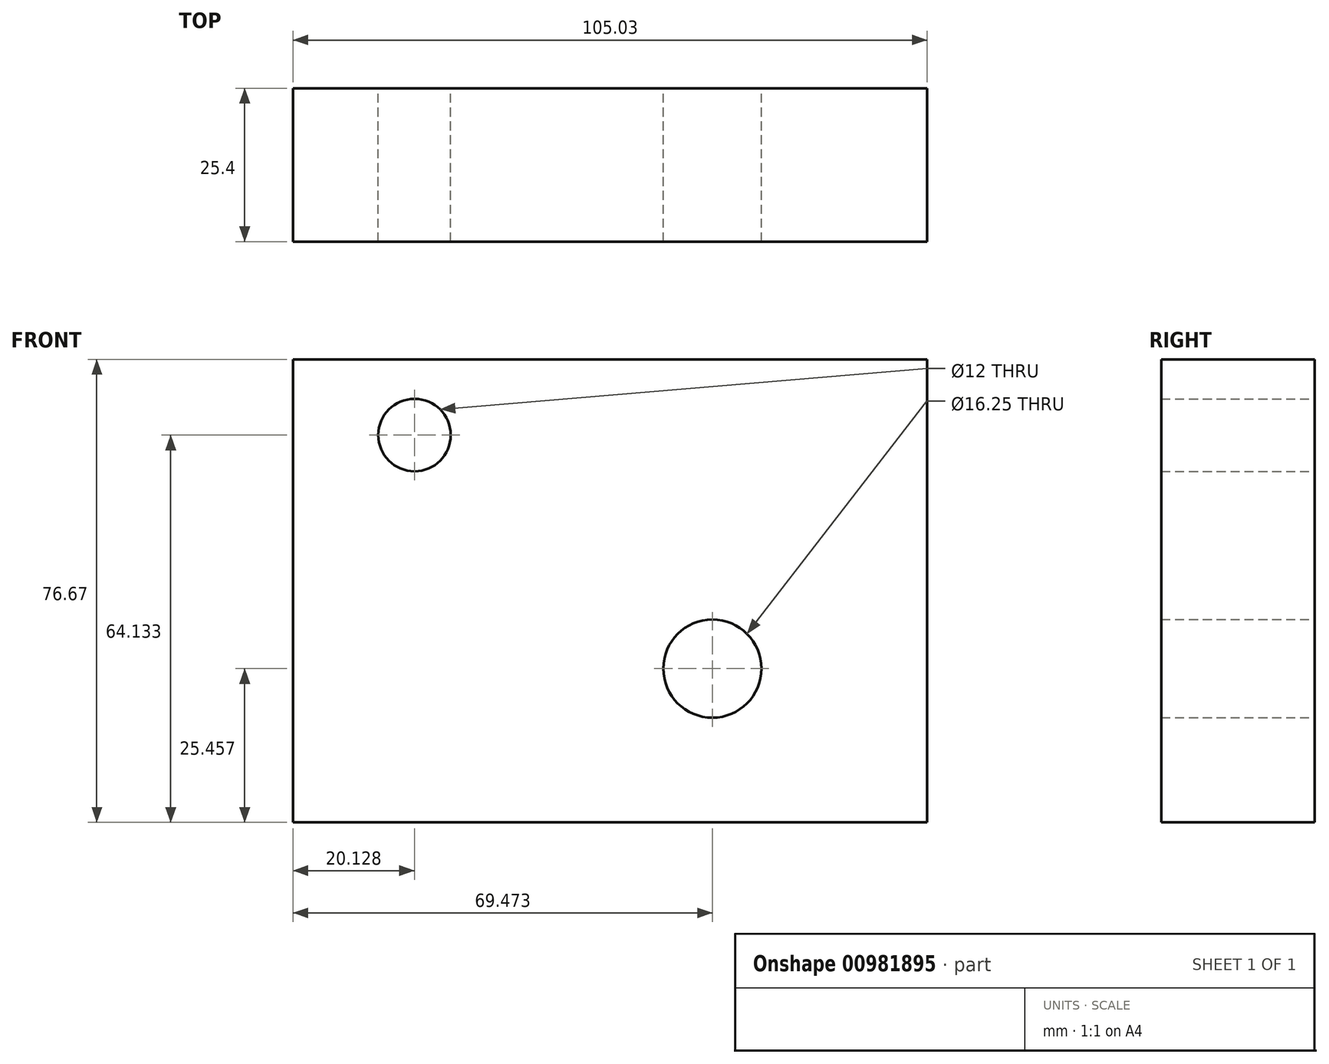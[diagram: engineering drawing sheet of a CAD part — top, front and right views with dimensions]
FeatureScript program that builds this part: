
annotation { "Feature Type Name" : "Feature", "Feature Type Description" : "" }
export const myFeature = defineFeature(function(context is Context, id is Id, definition is map)
    precondition{}
    {
        {
            var Q0;
            Q0=qCreatedBy(makeId("Front.planeOp"),FACE);
            var sketch = newSketch(context, id + "F0", { "sketchPlane" : qUnion([Q0])});
            skLineSegment(sketch, "E0.bottom", {"start": v(-51.98, 36.51) * mm, "end": v(53.05, 36.51) * mm});
            skLineSegment(sketch, "E0.top", {"start": v(-51.98, -40.16) * mm, "end": v(53.05, -40.16) * mm});
            skLineSegment(sketch, "E0.left", {"start": v(-51.98, 36.51) * mm, "end": v(-51.98, -40.16) * mm});
            skLineSegment(sketch, "E0.right", {"start": v(53.05, 36.51) * mm, "end": v(53.05, -40.16) * mm});
            skCircle(sketch, "E1", {"center": v(-31.85, 23.97) * mm, "radius": 6 * mm});
            skCircle(sketch, "E2", {"center": v(17.5, -14.7) * mm, "radius": 8.13 * mm});
            skSolve(sketch);
        }
        {
            var Q0;
            Q0 = qSketchRegion(id + "F0", true);
            extrude(context, id + "F1", {"entities" : qUnion([Q0]), "depth" : 25.4 * mm, "offsetDistance" : 25.4 * mm});
        }
    });
